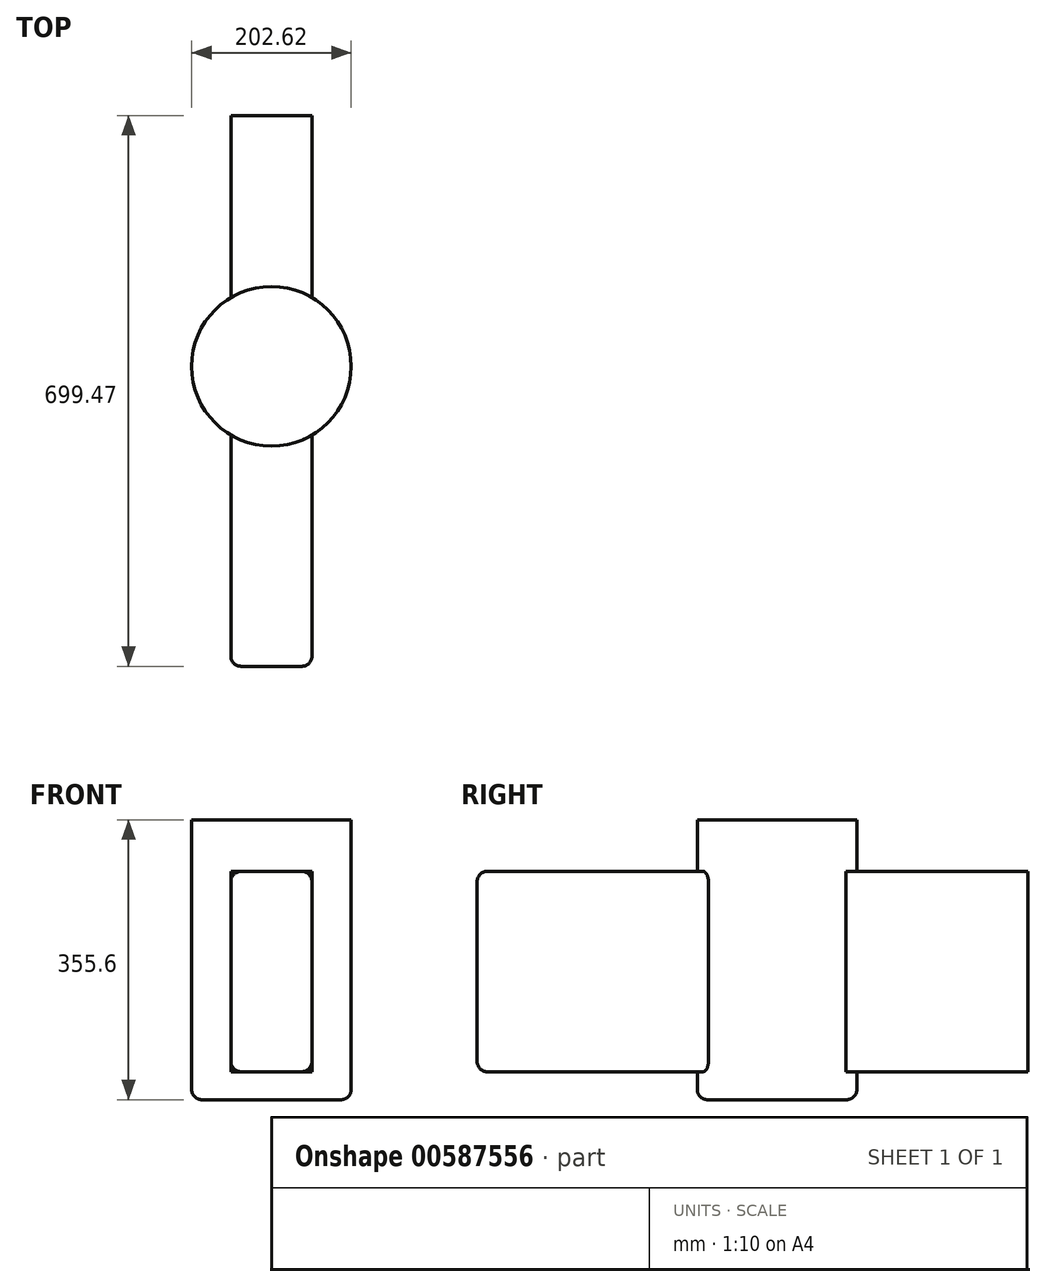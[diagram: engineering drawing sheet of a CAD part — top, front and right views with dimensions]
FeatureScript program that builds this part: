
annotation { "Feature Type Name" : "Feature", "Feature Type Description" : "" }
export const myFeature = defineFeature(function(context is Context, id is Id, definition is map)
    precondition{}
    {
        {
            var Q0;
            Q0=qCreatedBy(makeId("Top.planeOp"),FACE);
            var sketch = newSketch(context, id + "F0", { "sketchPlane" : qUnion([Q0])});
            skCircle(sketch, "E0", {"center": v(0, 0) * mm, "radius": 101.31 * mm});
            skSolve(sketch);
        }
        {
            var Q0;
            Q0 = qSketchRegion(id + "F0", true);
            extrude(context, id + "F1", {"entities" : qUnion([Q0]), "depth" : 355.6 * mm, "offsetDistance" : 25.4 * mm});
        }
        {
            var Q0;
            Q0=qCreatedBy(makeId("Front.planeOp"),FACE);
            var sketch = newSketch(context, id + "F2", { "sketchPlane" : qUnion([Q0])});
            skLineSegment(sketch, "E1.bottom", {"start": v(51.52, 289.9) * mm, "end": v(-51.52, 289.9) * mm});
            skLineSegment(sketch, "E1.top", {"start": v(51.52, 35.56) * mm, "end": v(-51.52, 35.56) * mm});
            skLineSegment(sketch, "E1.left", {"start": v(51.52, 289.9) * mm, "end": v(51.52, 35.56) * mm});
            skLineSegment(sketch, "E1.right", {"start": v(-51.52, 289.9) * mm, "end": v(-51.52, 35.56) * mm});
            skPoint(sketch, "E1.middle", {"position": v(0, 162.73) * mm});
            skSolve(sketch);
        }
        {
            var Q0;
            Q0 = qSketchRegion(id + "F2", true);
            extrude(context, id + "F3", {"entities" : qUnion([Q0]), "operationType" : NewBodyOperationType.ADD, "oppositeDirection" : true, "depth" : 318.47 * mm, "offsetDistance" : 25.4 * mm});
        }
        {
            var Q0;
            Q0 = qSketchRegion(id + "F2", true);
            extrude(context, id + "F4", {"entities" : qUnion([Q0]), "operationType" : NewBodyOperationType.ADD, "depth" : 381 * mm, "offsetDistance" : 25.4 * mm});
        }
        {
            var Q0;
            Q0=makeQuery(id+"F1.opExtrude","CAP_FACE",FACE,{"disambiguationData":[OSD([sQuery(id+"F0.wireOp",EDGE,"E0")])],"isStart":true});
            var Q1;
            Q1=makeQuery(id+"F4.opExtrude","SWEPT_EDGE",EDGE,{"disambiguationData":[OSD([sQuery(id+"F2.wireOp",EDGE,"E1.top"),sQuery(id+"F2.wireOp",EDGE,"E1.left")])]});
            var Q2;
            Q2=makeQuery(id+"F4.opExtrude","SWEPT_EDGE",EDGE,{"disambiguationData":[OSD([sQuery(id+"F2.wireOp",EDGE,"E1.bottom"),sQuery(id+"F2.wireOp",EDGE,"E1.left")])]});
            var Q3;
            Q3=makeQuery(id+"F4.opExtrude","CAP_EDGE",EDGE,{"disambiguationData":[OSD([sQuery(id+"F2.wireOp",EDGE,"E1.left")])],"isStart":false});
            var Q4;
            Q4=makeQuery(id+"F4.opExtrude","SWEPT_EDGE",EDGE,{"disambiguationData":[OSD([sQuery(id+"F2.wireOp",EDGE,"E1.top"),sQuery(id+"F2.wireOp",EDGE,"E1.right")])]});
            var Q5;
            Q5=makeQuery(id+"F4.opExtrude","SWEPT_EDGE",EDGE,{"disambiguationData":[OSD([sQuery(id+"F2.wireOp",EDGE,"E1.bottom"),sQuery(id+"F2.wireOp",EDGE,"E1.right")])]});
            var Q6;
            Q6=makeQuery(id+"F4.opExtrude","CAP_EDGE",EDGE,{"disambiguationData":[OSD([sQuery(id+"F2.wireOp",EDGE,"E1.bottom")])],"isStart":false});
            var Q7;
            Q7=makeQuery(id+"F4.opExtrude","CAP_EDGE",EDGE,{"disambiguationData":[OSD([sQuery(id+"F2.wireOp",EDGE,"E1.right")])],"isStart":false});
            var Q8;
            Q8=makeQuery(id+"F4.opExtrude","CAP_EDGE",EDGE,{"disambiguationData":[OSD([sQuery(id+"F2.wireOp",EDGE,"E1.top")])],"isStart":false});
            fillet(context, id + "F5", {"entities" : qUnion([Q0, Q1, Q2, Q3, Q4, Q5, Q6, Q7, Q8]), "radius" : 12.7 * mm, "tangentPropagation" : true, "allowEdgeOverflow" : false});
        }
    });
